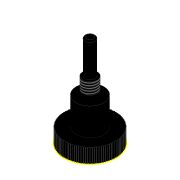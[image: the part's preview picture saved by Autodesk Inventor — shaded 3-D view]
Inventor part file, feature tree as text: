
AUTODESK INVENTOR PART (.ipt)
format: ipt  version: 2022.3 (Build 263350000, 350)  size: 715,776 bytes
history: native  units: mm
features: sketch x9, extrude x5, other x3, plane x2, fillet x2, loft x1, thread x1, projected_geometry x1
ambient origin geometry x8: Origin, YZ Plane, XZ Plane, XY Plane, X Axis, Y Axis, Z Axis, Center Point
bodies: Body1 (feature_tree)
feature tree (24):
  other  "Sólido1"
  extrude  "Extrusión1"  Depth=5.0mm TaperAngle=0.0deg
  extrude  "Extrusión2"  Depth=9.5mm TaperAngle=0.0deg
  sketch  "Boceto3"  dims[d6=-31.8mm d7=3.45mm]
  plane  "Plano de trabajo1"
  extrude  "Extrusión3"  Depth=3.45mm
  plane  "Plano de trabajo2"
  extrude  "Extrusión4"  [1 undecoded]
  sketch  "Boceto6"  dims[d16=0.0mm d17=90.0deg d18=4.0mm d19=0.0mm d20=0.5mm d21=1000.0mm d23=360.0deg]
  sketch  "Boceto7"  dims[d25=5.0mm d26=0.0mm]
  loft  "Solevación1"
  thread  "Rosca1"  [1 undecoded]
  extrude  "Extrusión5"  Depth=0.5mm TaperAngle=0.0deg
  fillet  "Empalme1"  Radius=0.5mm
  fillet  "Empalme2"  Radius=1000.0mm
  sketch  "Boceto9"  dims[d28=0.05mm]
  sketch  "Boceto1"  dims[d0=17.85mm d1=5.0mm d2=0.0mm]
  sketch  "Boceto2"  dims[d3=9.6mm d4=9.5mm d5=0.0mm]
  sketch  "Boceto4"  dims[d8=20.0mm d9=0.0mm d10=-11.7mm]
  sketch  "Boceto5"  dims[d11=5.0mm d12=4.0mm d13=0.0mm d14=0.0mm d15=90.0deg]
  other  "Aristas1"
  other  "Aristas2"
  sketch  "Boceto8"  dims[d27=0.5mm]
  projected_geometry  "Contorno proyectado1"
note: 2 required parameter values undecoded (feature->parameter linkage not recoverable at this tier; creation-order binding heuristic only, values carry confidence <= 0.55)
